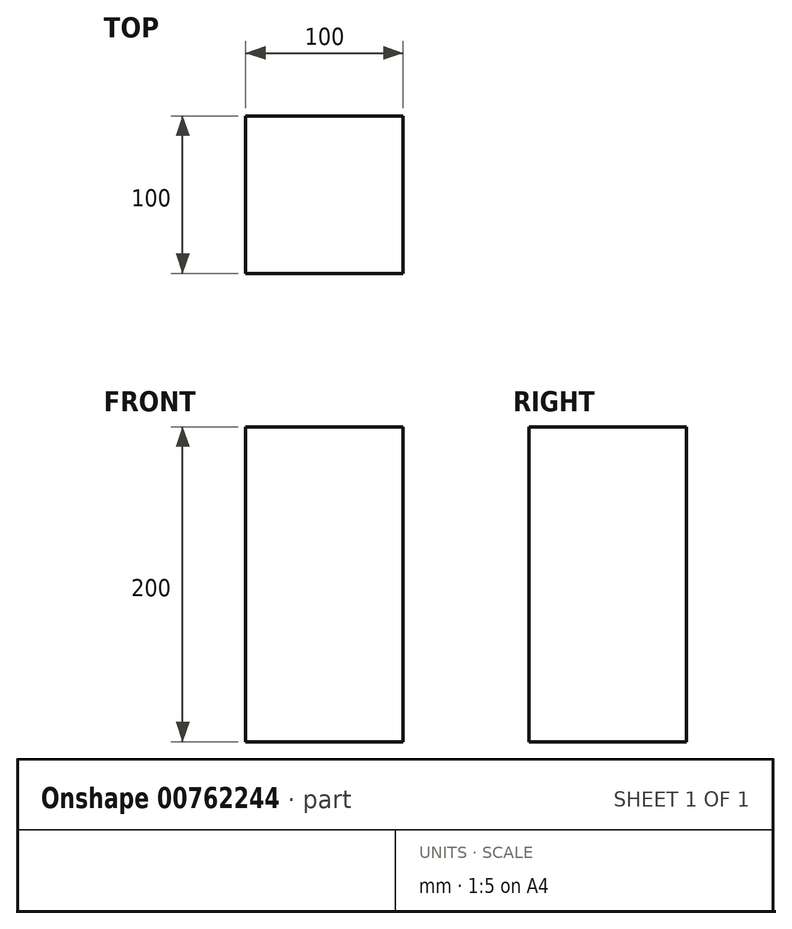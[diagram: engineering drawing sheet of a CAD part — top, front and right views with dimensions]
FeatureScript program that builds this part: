
annotation { "Feature Type Name" : "Feature", "Feature Type Description" : "" }
export const myFeature = defineFeature(function(context is Context, id is Id, definition is map)
    precondition{}
    {
        {
            var Q0;
            Q0=qCreatedBy(makeId("Top.planeOp"),FACE);
            var sketch = newSketch(context, id + "F0", { "sketchPlane" : qUnion([Q0])});
            skLineSegment(sketch, "E0.bottom", {"start": v(50, -50) * mm, "end": v(-50, -50) * mm});
            skLineSegment(sketch, "E0.top", {"start": v(50, 50) * mm, "end": v(-50, 50) * mm});
            skLineSegment(sketch, "E0.left", {"start": v(50, -50) * mm, "end": v(50, 50) * mm});
            skLineSegment(sketch, "E0.right", {"start": v(-50, -50) * mm, "end": v(-50, 50) * mm});
            skPoint(sketch, "E0.middle", {"position": v(0, 0) * mm});
            skSolve(sketch);
        }
        {
            var Q0;
            Q0=makeQuery(id+"F0.imprint","IMPRINT",FACE,{"disambiguationData":[TD([[makeQuery(id+"F0.imprint","IMPRINT",EDGE,{"derivedFrom":sQuery(id+"F0.wireOp",EDGE,"E0.bottom")}),-1.0]])]});
            extrude(context, id + "F1", {"entities" : qUnion([Q0]), "depth" : 200 * mm, "offsetDistance" : 25.4 * mm});
        }
    });
